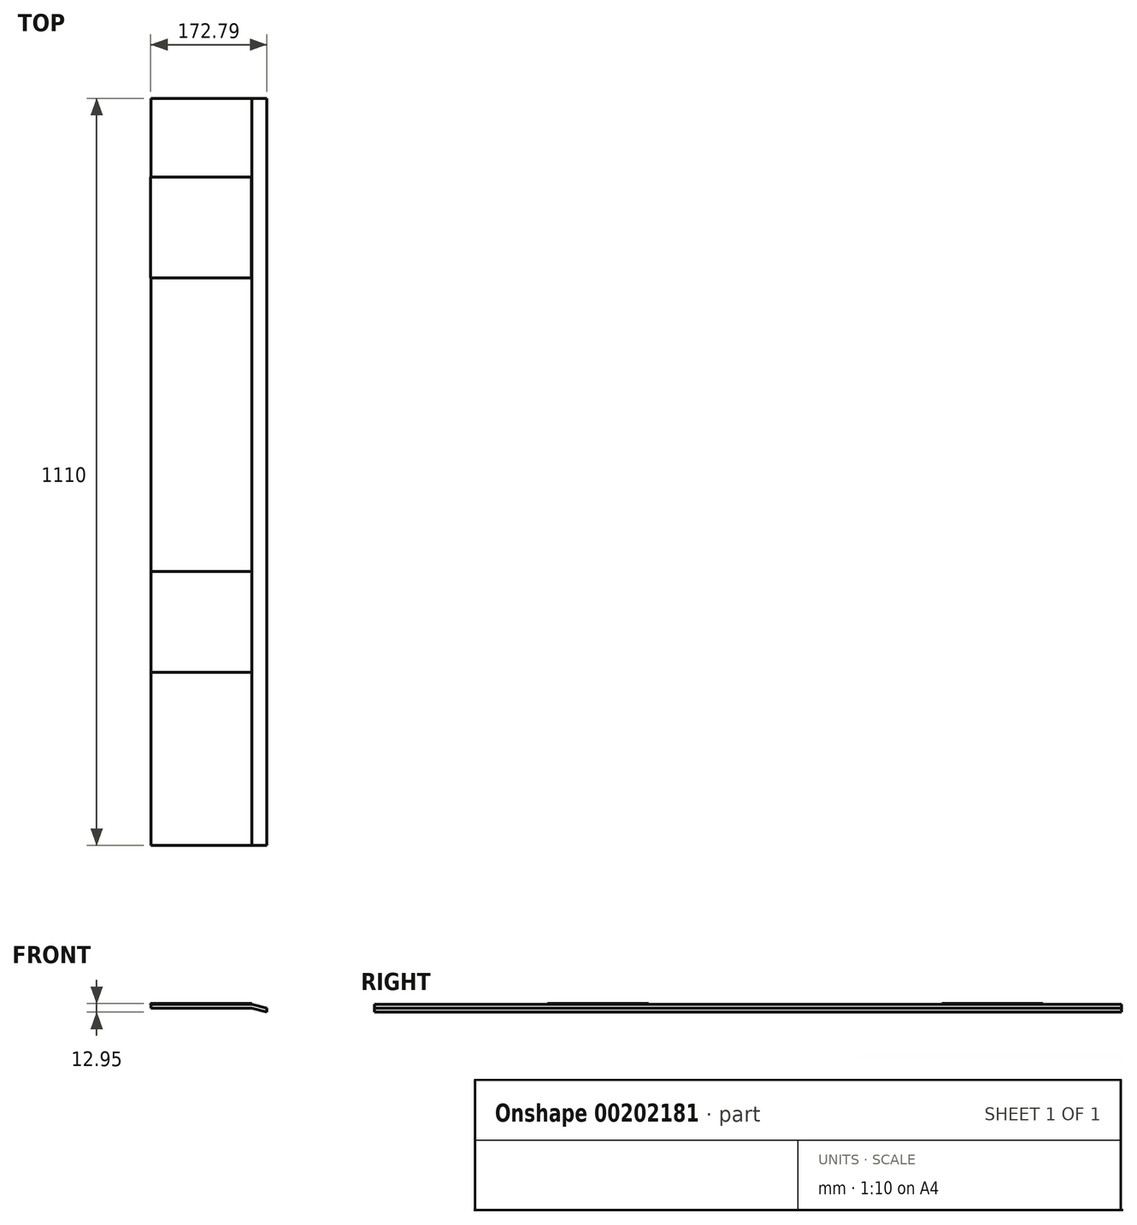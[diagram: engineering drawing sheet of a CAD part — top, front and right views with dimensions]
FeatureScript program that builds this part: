
annotation { "Feature Type Name" : "Feature", "Feature Type Description" : "" }
export const myFeature = defineFeature(function(context is Context, id is Id, definition is map)
    precondition{}
    {
        {
            var Q0;
            Q0=qCreatedBy(makeId("Front.planeOp"),FACE);
            var sketch = newSketch(context, id + "F0", { "sketchPlane" : qUnion([Q0])});
            skLineSegment(sketch, "E0", {"start": v(0, 0) * mm, "end": v(150, 0) * mm});
            skLineSegment(sketch, "E1", {"start": v(150, 0) * mm, "end": v(172.22, -5.95) * mm});
            skLineSegment(sketch, "E2", {"start": v(0, 0) * mm, "end": v(0, -6) * mm});
            skLineSegment(sketch, "E3", {"start": v(0, -6) * mm, "end": v(150, -6) * mm});
            skLineSegment(sketch, "E4", {"start": v(150, -6) * mm, "end": v(172.22, -11.95) * mm});
            skLineSegment(sketch, "E5", {"start": v(172.22, -11.95) * mm, "end": v(172.22, -5.95) * mm});
            skSolve(sketch);
        }
        {
            var Q0;
            Q0=makeQuery(id+"F0.imprint","IMPRINT",FACE,{"disambiguationData":[TD([[makeQuery(id+"F0.imprint","IMPRINT",EDGE,{"derivedFrom":sQuery(id+"F0.wireOp",EDGE,"E0")}),-1.0]])]});
            extrude(context, id + "F1", {"entities" : qUnion([Q0]), "depth" : 1110 * mm});
        }
        {
            var Q0;
            Q0=makeQuery(id+"F1.opExtrude","SWEPT_FACE",FACE,{"disambiguationData":[OSD([sQuery(id+"F0.wireOp",EDGE,"E0")])]});
            var sketch = newSketch(context, id + "F2", { "sketchPlane" : qUnion([Q0])});
            skLineSegment(sketch, "E6.bottom", {"start": v(149.43, -267.02) * mm, "end": v(-0.57, -267.02) * mm});
            skLineSegment(sketch, "E6.top", {"start": v(149.43, -117.02) * mm, "end": v(-0.57, -117.02) * mm});
            skLineSegment(sketch, "E6.left", {"start": v(149.43, -267.02) * mm, "end": v(149.43, -117.02) * mm});
            skLineSegment(sketch, "E6.right", {"start": v(-0.57, -267.02) * mm, "end": v(-0.57, -117.02) * mm});
            skPoint(sketch, "E6.middle", {"position": v(74.43, -192.02) * mm});
            skLineSegment(sketch, "E7.bottom", {"start": v(150, -852.97) * mm, "end": v(0, -852.97) * mm});
            skLineSegment(sketch, "E7.top", {"start": v(150, -702.97) * mm, "end": v(0, -702.97) * mm});
            skLineSegment(sketch, "E7.left", {"start": v(150, -852.97) * mm, "end": v(150, -702.97) * mm});
            skLineSegment(sketch, "E7.right", {"start": v(0, -852.97) * mm, "end": v(0, -702.97) * mm});
            skPoint(sketch, "E7.middle", {"position": v(75, -777.97) * mm});
            skSolve(sketch);
        }
        {
            var Q0;
            Q0=qSketchRegion(id+"F2",true);
            extrude(context, id + "F3", {"entities" : qUnion([Q0]), "operationType" : NewBodyOperationType.ADD, "depth" : 1 * mm});
        }
    });
